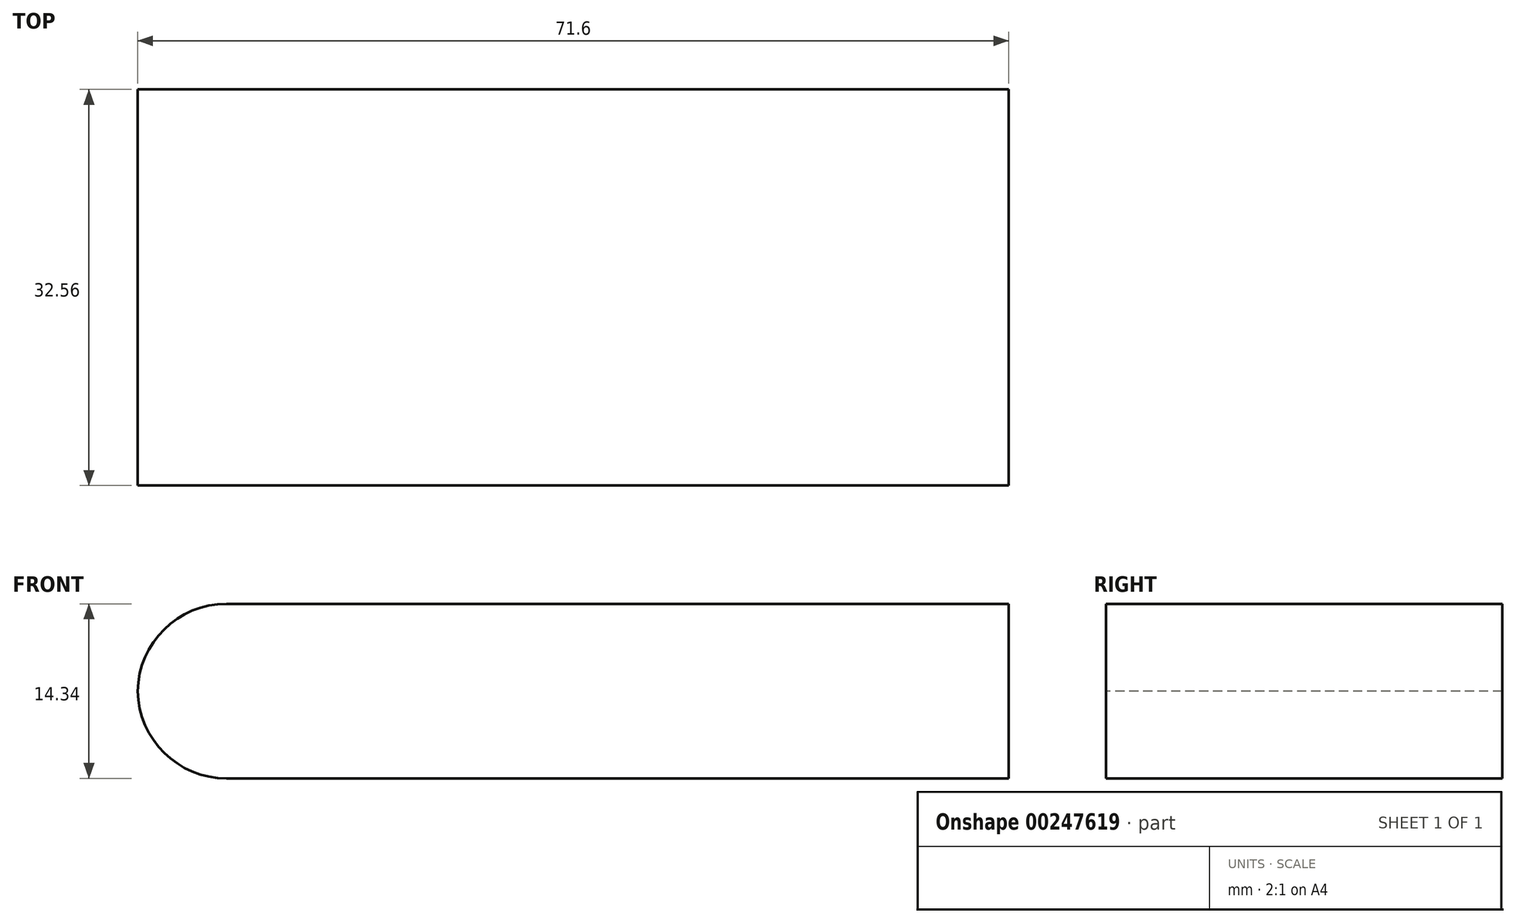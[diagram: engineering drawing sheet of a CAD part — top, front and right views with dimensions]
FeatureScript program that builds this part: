
annotation { "Feature Type Name" : "Feature", "Feature Type Description" : "" }
export const myFeature = defineFeature(function(context is Context, id is Id, definition is map)
    precondition{}
    {
        {
            var Q0;
            Q0=qCreatedBy(makeId("Front.planeOp"),FACE);
            var sketch = newSketch(context, id + "F0", { "sketchPlane" : qUnion([Q0])});
            skLineSegment(sketch, "E0.bottom", {"start": v(-35.8, 7.17) * mm, "end": v(35.8, 7.17) * mm});
            skLineSegment(sketch, "E0.top", {"start": v(-35.8, -7.17) * mm, "end": v(35.8, -7.17) * mm});
            skLineSegment(sketch, "E0.left", {"start": v(-35.8, 7.17) * mm, "end": v(-35.8, -7.17) * mm});
            skLineSegment(sketch, "E0.right", {"start": v(35.8, 7.17) * mm, "end": v(35.8, -7.18) * mm});
            skPoint(sketch, "E0.middle", {"position": v(0, 0) * mm});
            skSolve(sketch);
        }
        {
            var Q0;
            Q0 = qSketchRegion(id + "F0", true);
            var Q1;
            Q1=makeQuery(id+"F0.imprint","IMPRINT",FACE,{"disambiguationData":[TD([[makeQuery(id+"F0.imprint","IMPRINT",EDGE,{"derivedFrom":sQuery(id+"F0.wireOp",EDGE,"E0.bottom")}),-1.0]])]});
            extrude(context, id + "F1", {"entities" : qUnion([Q0, Q1]), "depth" : 32.56 * mm});
        }
        {
            var Q0;
            Q0=makeQuery(id+"F1.opExtrude","SWEPT_EDGE",EDGE,{"disambiguationData":[OSD([sQuery(id+"F0.wireOp",EDGE,"E0.bottom"),sQuery(id+"F0.wireOp",EDGE,"E0.left")])]});
            var Q1;
            Q1=makeQuery(id+"F1.opExtrude","SWEPT_EDGE",EDGE,{"disambiguationData":[OSD([sQuery(id+"F0.wireOp",EDGE,"E0.top"),sQuery(id+"F0.wireOp",EDGE,"E0.left")])]});
            fillet(context, id + "F2", {"entities" : qUnion([Q0, Q1]), "radius" : 7.3 * mm, "tangentPropagation" : true, "allowEdgeOverflow" : false});
        }
    });
